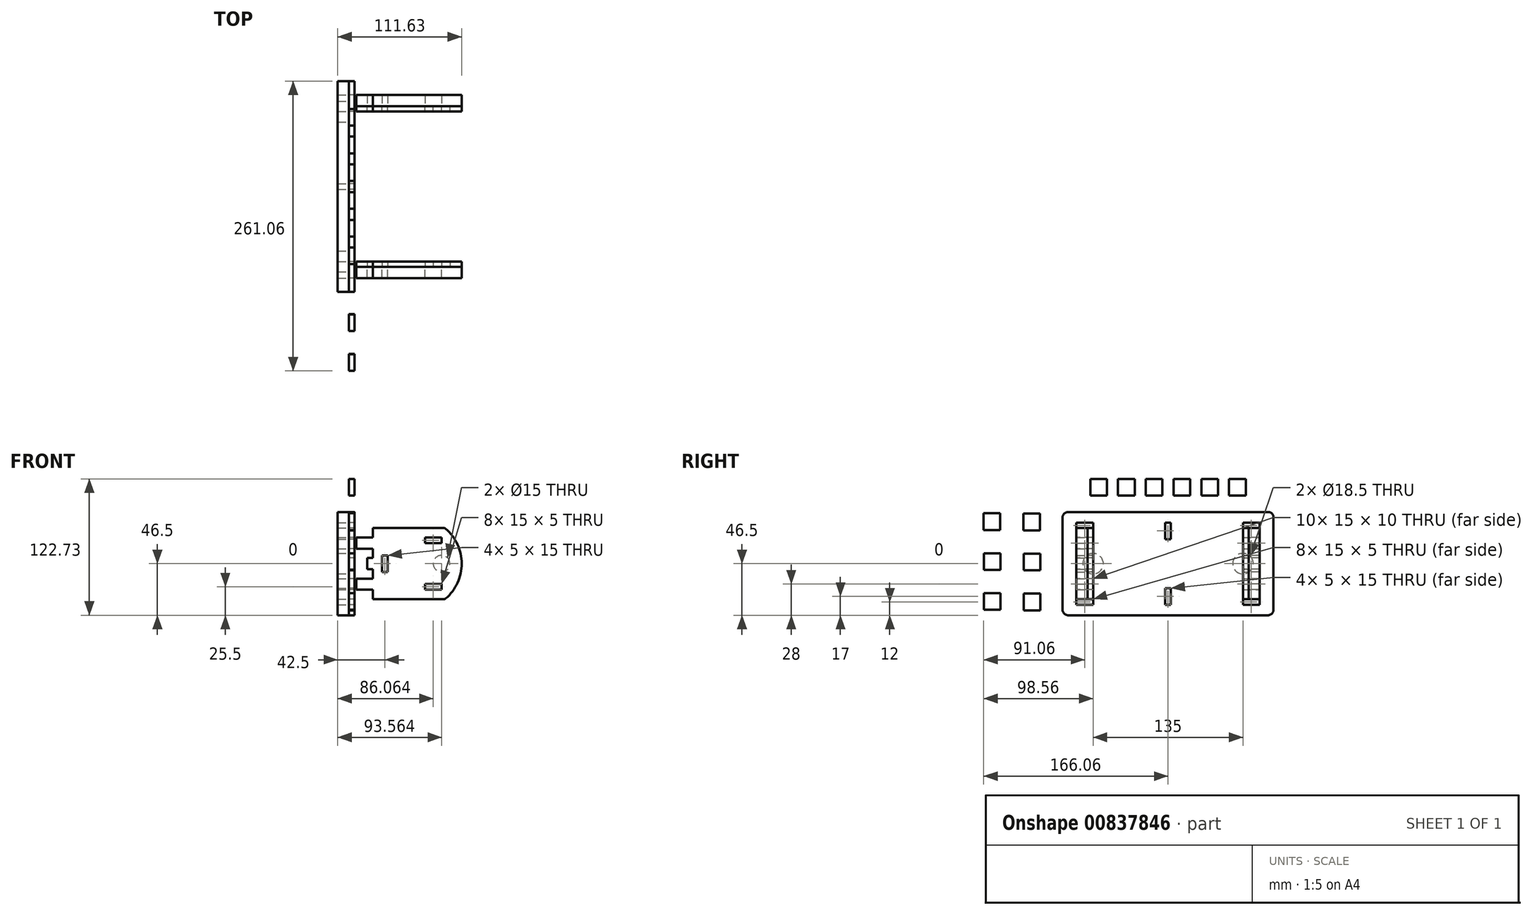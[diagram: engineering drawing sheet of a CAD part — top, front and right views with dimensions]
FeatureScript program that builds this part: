
annotation { "Feature Type Name" : "Feature", "Feature Type Description" : "" }
export const myFeature = defineFeature(function(context is Context, id is Id, definition is map)
    precondition{}
    {
        {
            var Q0;
            Q0=qCreatedBy(makeId("Right.planeOp"),FACE);
            var sketch = newSketch(context, id + "F0", { "sketchPlane" : qUnion([Q0])});
            skLineSegment(sketch, "E0.bottom", {"start": v(90, -46.5) * mm, "end": v(-90, -46.5) * mm});
            skLineSegment(sketch, "E0.top", {"start": v(90, 46.5) * mm, "end": v(-90, 46.5) * mm});
            skLineSegment(sketch, "E0.left", {"start": v(95, -41.5) * mm, "end": v(95, 41.5) * mm});
            skLineSegment(sketch, "E0.right", {"start": v(-95, -41.5) * mm, "end": v(-95, 41.5) * mm});
            skPoint(sketch, "E0.middle", {"position": v(0, 0) * mm});
            skLineSegment(sketch, "E1.bottom", {"start": v(67.5, 23.5) * mm, "end": v(82.5, 23.5) * mm});
            skLineSegment(sketch, "E1.top", {"start": v(67.5, 13.5) * mm, "end": v(82.5, 13.5) * mm});
            skLineSegment(sketch, "E1.left", {"start": v(67.5, 23.5) * mm, "end": v(67.5, 13.5) * mm});
            skLineSegment(sketch, "E1.right", {"start": v(82.5, 23.5) * mm, "end": v(82.5, 13.5) * mm});
            skLineSegment(sketch, "E2.bottom", {"start": v(67.5, -13.5) * mm, "end": v(82.5, -13.5) * mm});
            skLineSegment(sketch, "E2.top", {"start": v(67.5, -23.5) * mm, "end": v(82.5, -23.5) * mm});
            skLineSegment(sketch, "E2.left", {"start": v(67.5, -13.5) * mm, "end": v(67.5, -23.5) * mm});
            skLineSegment(sketch, "E2.right", {"start": v(82.5, -13.5) * mm, "end": v(82.5, -23.5) * mm});
            skLineSegment(sketch, "E3.bottom", {"start": v(-67.5, -13.5) * mm, "end": v(-82.5, -13.5) * mm});
            skLineSegment(sketch, "E3.top", {"start": v(-67.5, -23.5) * mm, "end": v(-82.5, -23.5) * mm});
            skLineSegment(sketch, "E3.left", {"start": v(-67.5, -13.5) * mm, "end": v(-67.5, -23.5) * mm});
            skLineSegment(sketch, "E3.right", {"start": v(-82.5, -13.5) * mm, "end": v(-82.5, -23.5) * mm});
            skLineSegment(sketch, "E4.bottom", {"start": v(-67.5, 13.5) * mm, "end": v(-82.5, 13.5) * mm});
            skLineSegment(sketch, "E4.top", {"start": v(-67.5, 23.5) * mm, "end": v(-82.5, 23.5) * mm});
            skLineSegment(sketch, "E4.left", {"start": v(-67.5, 13.5) * mm, "end": v(-67.5, 23.5) * mm});
            skLineSegment(sketch, "E4.right", {"start": v(-82.5, 13.5) * mm, "end": v(-82.5, 23.5) * mm});
            skPoint(sketch, "E5.visualSharp", {"position": v(-95, 46.5) * mm});
            skArc(sketch, "E5.filletArc", {"start": v(-90, 46.5) * mm, "mid": v(-93.54, 45.04) * mm, "end": v(-95, 41.5) * mm});
            skPoint(sketch, "E6.visualSharp", {"position": v(95, 46.5) * mm});
            skArc(sketch, "E6.filletArc", {"start": v(95, 41.5) * mm, "mid": v(93.54, 45.04) * mm, "end": v(90, 46.5) * mm});
            skPoint(sketch, "E7.visualSharp", {"position": v(95, -46.5) * mm});
            skArc(sketch, "E7.filletArc", {"start": v(90, -46.5) * mm, "mid": v(93.54, -45.04) * mm, "end": v(95, -41.5) * mm});
            skPoint(sketch, "E8.visualSharp", {"position": v(-95, -46.5) * mm});
            skArc(sketch, "E8.filletArc", {"start": v(-95, -41.5) * mm, "mid": v(-93.54, -45.04) * mm, "end": v(-90, -46.5) * mm});
            skCircle(sketch, "E9", {"center": v(-67.5, 0) * mm, "radius": 9.25 * mm});
            skCircle(sketch, "E10", {"center": v(67.5, 0) * mm, "radius": 9.25 * mm});
            skLineSegment(sketch, "E11.bottom", {"start": v(-67.5, 5) * mm, "end": v(-82.5, 5) * mm});
            skLineSegment(sketch, "E11.top", {"start": v(-67.5, -5) * mm, "end": v(-82.5, -5) * mm});
            skLineSegment(sketch, "E11.left", {"start": v(-67.5, 5) * mm, "end": v(-67.5, -5) * mm});
            skLineSegment(sketch, "E11.right", {"start": v(-82.5, 5) * mm, "end": v(-82.5, -5) * mm});
            skLineSegment(sketch, "E12.bottom", {"start": v(82.5, 5) * mm, "end": v(67.5, 5) * mm});
            skLineSegment(sketch, "E12.top", {"start": v(82.5, -5) * mm, "end": v(67.5, -5) * mm});
            skLineSegment(sketch, "E12.left", {"start": v(82.5, 5) * mm, "end": v(82.5, -5) * mm});
            skLineSegment(sketch, "E12.right", {"start": v(67.5, 5) * mm, "end": v(67.5, -5) * mm});
            skLineSegment(sketch, "E13.bottom", {"start": v(-67.5, 32) * mm, "end": v(-82.5, 32) * mm});
            skLineSegment(sketch, "E13.top", {"start": v(-67.5, 37) * mm, "end": v(-82.5, 37) * mm});
            skLineSegment(sketch, "E13.left", {"start": v(-67.5, 32) * mm, "end": v(-67.5, 37) * mm});
            skLineSegment(sketch, "E13.right", {"start": v(-82.5, 32) * mm, "end": v(-82.5, 37) * mm});
            skLineSegment(sketch, "E14.bottom", {"start": v(-82.5, -32) * mm, "end": v(-67.5, -32) * mm});
            skLineSegment(sketch, "E14.top", {"start": v(-82.5, -37) * mm, "end": v(-67.5, -37) * mm});
            skLineSegment(sketch, "E14.left", {"start": v(-82.5, -32) * mm, "end": v(-82.5, -37) * mm});
            skLineSegment(sketch, "E14.right", {"start": v(-67.5, -32) * mm, "end": v(-67.5, -37) * mm});
            skLineSegment(sketch, "E15.bottom", {"start": v(-70, 61.23) * mm, "end": v(-55, 61.23) * mm});
            skLineSegment(sketch, "E15.top", {"start": v(-70, 76.23) * mm, "end": v(-55, 76.23) * mm});
            skLineSegment(sketch, "E15.left", {"start": v(-70, 61.23) * mm, "end": v(-70, 76.23) * mm});
            skLineSegment(sketch, "E15.right", {"start": v(-55, 61.23) * mm, "end": v(-55, 76.23) * mm});
            skLineSegment(sketch, "E16.1.0.0", {"start": v(-45, 76.23) * mm, "end": v(-30, 76.23) * mm});
            skLineSegment(sketch, "E16.1.0.1", {"start": v(-30, 61.23) * mm, "end": v(-30, 76.23) * mm});
            skLineSegment(sketch, "E16.1.0.2", {"start": v(-45, 61.23) * mm, "end": v(-30, 61.23) * mm});
            skLineSegment(sketch, "E16.1.0.3", {"start": v(-45, 61.23) * mm, "end": v(-45, 76.23) * mm});
            skLineSegment(sketch, "E16.2.0.0", {"start": v(-20, 76.23) * mm, "end": v(-5, 76.23) * mm});
            skLineSegment(sketch, "E16.2.0.1", {"start": v(-5, 61.23) * mm, "end": v(-5, 76.23) * mm});
            skLineSegment(sketch, "E16.2.0.2", {"start": v(-20, 61.23) * mm, "end": v(-5, 61.23) * mm});
            skLineSegment(sketch, "E16.2.0.3", {"start": v(-20, 61.23) * mm, "end": v(-20, 76.23) * mm});
            skLineSegment(sketch, "E16.3.0.0", {"start": v(5, 76.23) * mm, "end": v(20, 76.23) * mm});
            skLineSegment(sketch, "E16.3.0.1", {"start": v(20, 61.23) * mm, "end": v(20, 76.23) * mm});
            skLineSegment(sketch, "E16.3.0.2", {"start": v(5, 61.23) * mm, "end": v(20, 61.23) * mm});
            skLineSegment(sketch, "E16.3.0.3", {"start": v(5, 61.23) * mm, "end": v(5, 76.23) * mm});
            skLineSegment(sketch, "E16.direction1", {"start": v(-70, 61.23) * mm, "end": v(-45, 61.23) * mm, "construction": true});
            skLineSegment(sketch, "E17.bottom", {"start": v(67.5, 37) * mm, "end": v(82.5, 37) * mm});
            skLineSegment(sketch, "E17.top", {"start": v(67.5, 32) * mm, "end": v(82.5, 32) * mm});
            skLineSegment(sketch, "E17.left", {"start": v(67.5, 37) * mm, "end": v(67.5, 32) * mm});
            skLineSegment(sketch, "E17.right", {"start": v(82.5, 37) * mm, "end": v(82.5, 32) * mm});
            skLineSegment(sketch, "E18.bottom", {"start": v(67.5, -32) * mm, "end": v(82.5, -32) * mm});
            skLineSegment(sketch, "E18.top", {"start": v(67.5, -37) * mm, "end": v(82.5, -37) * mm});
            skLineSegment(sketch, "E18.left", {"start": v(67.5, -32) * mm, "end": v(67.5, -37) * mm});
            skLineSegment(sketch, "E18.right", {"start": v(82.5, -32) * mm, "end": v(82.5, -37) * mm});
            skLineSegment(sketch, "E19.0.4.0", {"start": v(30, 76.23) * mm, "end": v(45, 76.23) * mm});
            skLineSegment(sketch, "E19.3.4.0", {"start": v(45, 61.23) * mm, "end": v(45, 76.23) * mm});
            skLineSegment(sketch, "E19.6.4.0", {"start": v(30, 61.23) * mm, "end": v(45, 61.23) * mm});
            skLineSegment(sketch, "E19.9.4.0", {"start": v(30, 61.23) * mm, "end": v(30, 76.23) * mm});
            skLineSegment(sketch, "E19.0.5.0", {"start": v(55, 76.23) * mm, "end": v(70, 76.23) * mm});
            skLineSegment(sketch, "E19.3.5.0", {"start": v(70, 61.23) * mm, "end": v(70, 76.23) * mm});
            skLineSegment(sketch, "E19.6.5.0", {"start": v(55, 61.23) * mm, "end": v(70, 61.23) * mm});
            skLineSegment(sketch, "E19.9.5.0", {"start": v(55, 61.23) * mm, "end": v(55, 76.23) * mm});
            skLineSegment(sketch, "E20.bottom", {"start": v(-115.17, 45) * mm, "end": v(-130.17, 45) * mm});
            skLineSegment(sketch, "E20.top", {"start": v(-115.17, 30) * mm, "end": v(-130.17, 30) * mm});
            skLineSegment(sketch, "E20.left", {"start": v(-115.17, 45) * mm, "end": v(-115.17, 30) * mm});
            skLineSegment(sketch, "E20.right", {"start": v(-130.17, 45) * mm, "end": v(-130.17, 30) * mm});
            skLineSegment(sketch, "E21.0.1.0", {"start": v(-115.03, 9) * mm, "end": v(-115.03, -6) * mm});
            skLineSegment(sketch, "E21.0.1.1", {"start": v(-115.03, 9) * mm, "end": v(-130.03, 9) * mm});
            skLineSegment(sketch, "E21.0.1.2", {"start": v(-130.03, 9) * mm, "end": v(-130.03, -6) * mm});
            skLineSegment(sketch, "E21.0.1.3", {"start": v(-115.03, -6) * mm, "end": v(-130.03, -6) * mm});
            skLineSegment(sketch, "E21.1.0.0", {"start": v(-151.06, 45.35) * mm, "end": v(-151.06, 30.35) * mm});
            skLineSegment(sketch, "E21.1.0.1", {"start": v(-151.06, 45.35) * mm, "end": v(-166.06, 45.35) * mm});
            skLineSegment(sketch, "E21.1.0.2", {"start": v(-166.06, 45.35) * mm, "end": v(-166.06, 30.35) * mm});
            skLineSegment(sketch, "E21.1.0.3", {"start": v(-151.06, 30.35) * mm, "end": v(-166.06, 30.35) * mm});
            skLineSegment(sketch, "E21.1.1.0", {"start": v(-150.92, 9.35) * mm, "end": v(-150.92, -5.65) * mm});
            skLineSegment(sketch, "E21.1.1.1", {"start": v(-150.92, 9.35) * mm, "end": v(-165.92, 9.35) * mm});
            skLineSegment(sketch, "E21.1.1.2", {"start": v(-165.92, 9.35) * mm, "end": v(-165.92, -5.65) * mm});
            skLineSegment(sketch, "E21.1.1.3", {"start": v(-150.92, -5.65) * mm, "end": v(-165.92, -5.65) * mm});
            skLineSegment(sketch, "E21.direction1", {"start": v(-115.17, 30) * mm, "end": v(-151.06, 30.35) * mm, "construction": true});
            skLineSegment(sketch, "E21.direction2", {"start": v(-115.17, 30) * mm, "end": v(-115.03, -6) * mm, "construction": true});
            skLineSegment(sketch, "E22.0.0.2", {"start": v(-114.89, -27) * mm, "end": v(-114.89, -42) * mm});
            skLineSegment(sketch, "E22.3.0.2", {"start": v(-114.89, -27) * mm, "end": v(-129.89, -27) * mm});
            skLineSegment(sketch, "E22.6.0.2", {"start": v(-129.89, -27) * mm, "end": v(-129.89, -42) * mm});
            skLineSegment(sketch, "E22.9.0.2", {"start": v(-114.89, -42) * mm, "end": v(-129.89, -42) * mm});
            skLineSegment(sketch, "E22.0.1.2", {"start": v(-150.78, -26.65) * mm, "end": v(-150.78, -41.65) * mm});
            skLineSegment(sketch, "E22.3.1.2", {"start": v(-150.78, -26.65) * mm, "end": v(-165.78, -26.65) * mm});
            skLineSegment(sketch, "E22.6.1.2", {"start": v(-165.78, -26.65) * mm, "end": v(-165.78, -41.65) * mm});
            skLineSegment(sketch, "E22.9.1.2", {"start": v(-150.78, -41.65) * mm, "end": v(-165.78, -41.65) * mm});
            skLineSegment(sketch, "E23.1.0", {"start": v(2.5, 22) * mm, "end": v(2.5, 37) * mm});
            skLineSegment(sketch, "E23.1.1", {"start": v(-2.5, 22) * mm, "end": v(-2.5, 37) * mm});
            skLineSegment(sketch, "E23.1.2", {"start": v(-2.5, 37) * mm, "end": v(2.5, 37) * mm});
            skLineSegment(sketch, "E23.1.3", {"start": v(-2.5, 22) * mm, "end": v(2.5, 22) * mm});
            skLineSegment(sketch, "E23.3.0", {"start": v(-2.5, -22) * mm, "end": v(-2.5, -37) * mm});
            skLineSegment(sketch, "E23.3.1", {"start": v(2.5, -22) * mm, "end": v(2.5, -37) * mm});
            skLineSegment(sketch, "E23.3.2", {"start": v(2.5, -37) * mm, "end": v(-2.5, -37) * mm});
            skLineSegment(sketch, "E23.3.3", {"start": v(2.5, -22) * mm, "end": v(-2.5, -22) * mm});
            skSolve(sketch);
        }
        {
            var Q0;
            Q0=makeQuery(id+"F0.imprint","IMPRINT",FACE,{"disambiguationData":[TD([[makeQuery(id+"F0.imprint","IMPRINT",EDGE,{"derivedFrom":sQuery(id+"F0.wireOp",EDGE,"E0.bottom")}),-1.0]])]});
            var Q1;
            {var subQ5=sQuery(id+"F0.wireOp",EDGE,"E11.left");Q1=makeQuery(id+"F0.imprint","IMPRINT",FACE,{"disambiguationData":[TD([[makeQuery(id+"F0.imprint","IMPRINT",EDGE,{"derivedFrom":subQ5}),1.0]])]});}
            var Q2;
            {var subQ5=sQuery(id+"F0.wireOp",EDGE,"E12.right");Q2=makeQuery(id+"F0.imprint","IMPRINT",FACE,{"disambiguationData":[TD([[makeQuery(id+"F0.imprint","IMPRINT",EDGE,{"derivedFrom":subQ5}),-1.0]])]});}
            var Q3;
            Q3=makeQuery(id+"F0.imprint","IMPRINT",FACE,{"disambiguationData":[TD([[makeQuery(id+"F0.imprint","IMPRINT",EDGE,{"derivedFrom":sQuery(id+"F0.wireOp",EDGE,"E21.1.0.0")}),-1.0]])]});
            var Q4;
            Q4=makeQuery(id+"F0.imprint","IMPRINT",FACE,{"disambiguationData":[TD([[makeQuery(id+"F0.imprint","IMPRINT",EDGE,{"derivedFrom":sQuery(id+"F0.wireOp",EDGE,"E20.bottom")}),1.0]])]});
            var Q5;
            Q5=makeQuery(id+"F0.imprint","IMPRINT",FACE,{"disambiguationData":[TD([[makeQuery(id+"F0.imprint","IMPRINT",EDGE,{"derivedFrom":sQuery(id+"F0.wireOp",EDGE,"E21.1.1.0")}),-1.0]])]});
            var Q6;
            Q6=makeQuery(id+"F0.imprint","IMPRINT",FACE,{"disambiguationData":[TD([[makeQuery(id+"F0.imprint","IMPRINT",EDGE,{"derivedFrom":sQuery(id+"F0.wireOp",EDGE,"E21.0.1.0")}),-1.0]])]});
            var Q7;
            Q7=makeQuery(id+"F0.imprint","IMPRINT",FACE,{"disambiguationData":[TD([[makeQuery(id+"F0.imprint","IMPRINT",EDGE,{"derivedFrom":sQuery(id+"F0.wireOp",EDGE,"E22.0.1.2")}),-1.0]])]});
            var Q8;
            Q8=makeQuery(id+"F0.imprint","IMPRINT",FACE,{"disambiguationData":[TD([[makeQuery(id+"F0.imprint","IMPRINT",EDGE,{"derivedFrom":sQuery(id+"F0.wireOp",EDGE,"E22.0.0.2")}),-1.0]])]});
            var Q9;
            Q9=makeQuery(id+"F0.imprint","IMPRINT",FACE,{"disambiguationData":[TD([[makeQuery(id+"F0.imprint","IMPRINT",EDGE,{"derivedFrom":sQuery(id+"F0.wireOp",EDGE,"E15.bottom")}),1.0]])]});
            var Q10;
            Q10=makeQuery(id+"F0.imprint","IMPRINT",FACE,{"disambiguationData":[TD([[makeQuery(id+"F0.imprint","IMPRINT",EDGE,{"derivedFrom":sQuery(id+"F0.wireOp",EDGE,"E16.1.0.0")}),-1.0]])]});
            var Q11;
            Q11=makeQuery(id+"F0.imprint","IMPRINT",FACE,{"disambiguationData":[TD([[makeQuery(id+"F0.imprint","IMPRINT",EDGE,{"derivedFrom":sQuery(id+"F0.wireOp",EDGE,"E16.2.0.0")}),-1.0]])]});
            var Q12;
            Q12=makeQuery(id+"F0.imprint","IMPRINT",FACE,{"disambiguationData":[TD([[makeQuery(id+"F0.imprint","IMPRINT",EDGE,{"derivedFrom":sQuery(id+"F0.wireOp",EDGE,"E16.3.0.0")}),-1.0]])]});
            var Q13;
            Q13=makeQuery(id+"F0.imprint","IMPRINT",FACE,{"disambiguationData":[TD([[makeQuery(id+"F0.imprint","IMPRINT",EDGE,{"derivedFrom":sQuery(id+"F0.wireOp",EDGE,"E19.0.4.0")}),-1.0]])]});
            var Q14;
            Q14=makeQuery(id+"F0.imprint","IMPRINT",FACE,{"disambiguationData":[TD([[makeQuery(id+"F0.imprint","IMPRINT",EDGE,{"derivedFrom":sQuery(id+"F0.wireOp",EDGE,"E19.0.5.0")}),-1.0]])]});
            extrude(context, id + "F1", {"entities" : qUnion([Q0, Q1, Q2, Q3, Q4, Q5, Q6, Q7, Q8, Q9, Q10, Q11, Q12, Q13, Q14]), "depth" : 5 * mm, "offsetDistance" : 25 * mm});
        }
        {
            var Q0;
            Q0=makeQuery(id+"F0.imprint","IMPRINT",FACE,{"disambiguationData":[TD([[makeQuery(id+"F0.imprint","IMPRINT",EDGE,{"derivedFrom":sQuery(id+"F0.wireOp",EDGE,"E0.bottom")}),-1.0]])]});
            var Q1;
            {var subQ5=sQuery(id+"F0.wireOp",EDGE,"E12.left");Q1=makeQuery(id+"F0.imprint","IMPRINT",FACE,{"disambiguationData":[TD([[makeQuery(id+"F0.imprint","IMPRINT",EDGE,{"derivedFrom":subQ5}),-1.0]])]});}
            var Q2;
            {var subQ5=sQuery(id+"F0.wireOp",EDGE,"E11.right");Q2=makeQuery(id+"F0.imprint","IMPRINT",FACE,{"disambiguationData":[TD([[makeQuery(id+"F0.imprint","IMPRINT",EDGE,{"derivedFrom":subQ5}),1.0]])]});}
            var Q3;
            Q3=makeQuery(id+"F0.imprint","IMPRINT",FACE,{"disambiguationData":[TD([[makeQuery(id+"F0.imprint","IMPRINT",EDGE,{"derivedFrom":sQuery(id+"F0.wireOp",EDGE,"2e16871f-ea5c-4dd4-b328-3b17c4bea811.0.6.0")}),-1.0]])]});
            var Q4;
            Q4=makeQuery(id+"F0.imprint","IMPRINT",FACE,{"disambiguationData":[TD([[makeQuery(id+"F0.imprint","IMPRINT",EDGE,{"derivedFrom":sQuery(id+"F0.wireOp",EDGE,"2e16871f-ea5c-4dd4-b328-3b17c4bea811.0.7.0")}),-1.0]])]});
            var Q5;
            Q5=makeQuery(id+"F0.imprint","IMPRINT",FACE,{"disambiguationData":[TD([[makeQuery(id+"F0.imprint","IMPRINT",EDGE,{"derivedFrom":sQuery(id+"F0.wireOp",EDGE,"2e16871f-ea5c-4dd4-b328-3b17c4bea811.0.8.0")}),-1.0]])]});
            extrude(context, id + "F2", {"entities" : qUnion([Q0, Q1, Q2, Q3, Q4, Q5]), "oppositeDirection" : true, "depth" : 10 * mm, "offsetDistance" : 25 * mm});
        }
        {
            var Q0;
            Q0=qCreatedBy(makeId("Front.planeOp"),FACE);
            cPlane(context, id + "F3", {"entities" : qUnion([Q0]), "cplaneType" : CPlaneType.OFFSET, "offset" : 72.5 * mm, "width" : 150 * mm, "height" : 150 * mm});
        }
        {
            var Q0;
            Q0=qCreatedBy(id+"F3.planeOp",FACE);
            var sketch = newSketch(context, id + "F4", { "sketchPlane" : qUnion([Q0])});
            skLineSegment(sketch, "E24", {"start": v(85.9, 32) * mm, "end": v(21.63, 32) * mm});
            skLineSegment(sketch, "E25", {"start": v(21.63, 32) * mm, "end": v(21.63, 23.5) * mm});
            skLineSegment(sketch, "E26", {"start": v(21.63, 23.5) * mm, "end": v(6.63, 23.5) * mm});
            skLineSegment(sketch, "E27", {"start": v(6.63, 23.5) * mm, "end": v(6.63, 13.5) * mm});
            skLineSegment(sketch, "E28", {"start": v(6.63, 13.5) * mm, "end": v(21.63, 13.5) * mm});
            skLineSegment(sketch, "E29", {"start": v(21.63, -13.5) * mm, "end": v(6.63, -13.5) * mm});
            skLineSegment(sketch, "E30", {"start": v(6.63, -13.5) * mm, "end": v(6.63, -23.5) * mm});
            skLineSegment(sketch, "E31", {"start": v(6.63, -23.5) * mm, "end": v(21.63, -23.5) * mm});
            skLineSegment(sketch, "E32", {"start": v(21.63, -23.5) * mm, "end": v(21.63, -32) * mm});
            skLineSegment(sketch, "E33", {"start": v(21.63, -32) * mm, "end": v(85.9, -32) * mm});
            skPoint(sketch, "E34", {"position": v(101.63, 0) * mm});
            skArc(sketch, "E35", {"start": v(87.2, -31.51) * mm, "mid": v(101.63, 0) * mm, "end": v(87.2, 31.51) * mm});
            skPoint(sketch, "E36.visualSharp", {"position": v(86.63, 32) * mm});
            skArc(sketch, "E36.filletArc", {"start": v(87.2, 31.51) * mm, "mid": v(86.6, 31.87) * mm, "end": v(85.9, 32) * mm});
            skPoint(sketch, "E37.visualSharp", {"position": v(86.63, -32) * mm});
            skArc(sketch, "E37.filletArc", {"start": v(85.9, -32) * mm, "mid": v(86.6, -31.87) * mm, "end": v(87.2, -31.51) * mm});
            skCircle(sketch, "E38", {"center": v(83.56, 0) * mm, "radius": 7.5 * mm});
            skLineSegment(sketch, "E39", {"start": v(21.63, 13.5) * mm, "end": v(21.63, 5) * mm});
            skLineSegment(sketch, "E40", {"start": v(21.63, 5) * mm, "end": v(16.63, 5) * mm});
            skLineSegment(sketch, "E41", {"start": v(16.63, 5) * mm, "end": v(16.63, -5) * mm});
            skLineSegment(sketch, "E42", {"start": v(16.63, -5) * mm, "end": v(21.63, -5) * mm});
            skLineSegment(sketch, "E43", {"start": v(21.63, -5) * mm, "end": v(21.63, -13.5) * mm});
            skLineSegment(sketch, "E44.bottom", {"start": v(83.56, 23.5) * mm, "end": v(68.56, 23.5) * mm});
            skLineSegment(sketch, "E44.top", {"start": v(83.56, 18.5) * mm, "end": v(68.56, 18.5) * mm});
            skLineSegment(sketch, "E44.left", {"start": v(83.56, 23.5) * mm, "end": v(83.56, 18.5) * mm});
            skLineSegment(sketch, "E44.right", {"start": v(68.56, 23.5) * mm, "end": v(68.56, 18.5) * mm});
            skLineSegment(sketch, "E45.bottom", {"start": v(83.56, -18.5) * mm, "end": v(68.56, -18.5) * mm});
            skLineSegment(sketch, "E45.top", {"start": v(83.56, -23.5) * mm, "end": v(68.56, -23.5) * mm});
            skLineSegment(sketch, "E45.left", {"start": v(83.56, -18.5) * mm, "end": v(83.56, -23.5) * mm});
            skLineSegment(sketch, "E45.right", {"start": v(68.56, -18.5) * mm, "end": v(68.56, -23.5) * mm});
            skLineSegment(sketch, "E46.bottom", {"start": v(30, 7.5) * mm, "end": v(35, 7.5) * mm});
            skLineSegment(sketch, "E46.top", {"start": v(30, -7.5) * mm, "end": v(35, -7.5) * mm});
            skLineSegment(sketch, "E46.left", {"start": v(30, 7.5) * mm, "end": v(30, -7.5) * mm});
            skLineSegment(sketch, "E46.right", {"start": v(35, 7.5) * mm, "end": v(35, -7.5) * mm});
            skSolve(sketch);
        }
        {
            var Q0;
            Q0=makeQuery(id+"F4.imprint","IMPRINT",FACE,{"disambiguationData":[TD([[makeQuery(id+"F4.imprint","IMPRINT",EDGE,{"derivedFrom":sQuery(id+"F4.wireOp",EDGE,"E24")}),1.0]])]});
            extrude(context, id + "F5", {"entities" : qUnion([Q0]), "oppositeDirection" : true, "depth" : 5 * mm, "offsetDistance" : 25 * mm});
        }
        {
            var Q0;
            Q0=makeQuery(id+"F4.imprint","IMPRINT",FACE,{"disambiguationData":[TD([[makeQuery(id+"F4.imprint","IMPRINT",EDGE,{"derivedFrom":sQuery(id+"F4.wireOp",EDGE,"E24")}),1.0]])]});
            var Q1;
            Q1=makeQuery(id+"F4.imprint","IMPRINT",FACE,{"disambiguationData":[TD([[makeQuery(id+"F4.imprint","IMPRINT",EDGE,{"derivedFrom":sQuery(id+"F4.wireOp",EDGE,"E38")}),1.0]])]});
            extrude(context, id + "F6", {"entities" : qUnion([Q0, Q1]), "depth" : 10 * mm, "offsetDistance" : 25 * mm});
        }
        {
            var Q0;
            Q0=qCreatedBy(makeId("Top.planeOp"),FACE);
            var sketch = newSketch(context, id + "F7", { "sketchPlane" : qUnion([Q0])});
            skLineSegment(sketch, "E47", {"start": v(0, 0) * mm, "end": v(159.96, 0) * mm, "construction": true});
            skSolve(sketch);
        }
        {
            var Q0;
            Q0=makeQuery(id+"F5.opExtrude","SWEPT_BODY",BODY,{"disambiguationData":[OSD([sQuery(id+"F4.wireOp",EDGE,"E24"),sQuery(id+"F4.wireOp",EDGE,"E25"),sQuery(id+"F4.wireOp",EDGE,"E26"),sQuery(id+"F4.wireOp",EDGE,"E27"),sQuery(id+"F4.wireOp",EDGE,"E28"),sQuery(id+"F4.wireOp",EDGE,"E29"),sQuery(id+"F4.wireOp",EDGE,"E30"),sQuery(id+"F4.wireOp",EDGE,"E31"),sQuery(id+"F4.wireOp",EDGE,"E32"),sQuery(id+"F4.wireOp",EDGE,"E33"),sQuery(id+"F4.wireOp",EDGE,"E35"),sQuery(id+"F4.wireOp",EDGE,"E36.filletArc"),sQuery(id+"F4.wireOp",EDGE,"E37.filletArc"),sQuery(id+"F4.wireOp",EDGE,"E38"),sQuery(id+"F4.wireOp",EDGE,"E39"),sQuery(id+"F4.wireOp",EDGE,"E40"),sQuery(id+"F4.wireOp",EDGE,"E41"),sQuery(id+"F4.wireOp",EDGE,"E42"),sQuery(id+"F4.wireOp",EDGE,"E43"),sQuery(id+"F4.wireOp",EDGE,"E44.bottom"),sQuery(id+"F4.wireOp",EDGE,"E44.top"),sQuery(id+"F4.wireOp",EDGE,"E44.left"),sQuery(id+"F4.wireOp",EDGE,"E44.right"),sQuery(id+"F4.wireOp",EDGE,"E45.bottom"),sQuery(id+"F4.wireOp",EDGE,"E45.top"),sQuery(id+"F4.wireOp",EDGE,"E45.left"),sQuery(id+"F4.wireOp",EDGE,"E45.right"),sQuery(id+"F4.wireOp",EDGE,"E46.bottom"),sQuery(id+"F4.wireOp",EDGE,"E46.top"),sQuery(id+"F4.wireOp",EDGE,"E46.left"),sQuery(id+"F4.wireOp",EDGE,"E46.right")])]});
            var Q1;
            Q1=makeQuery(id+"F6.opExtrude","SWEPT_BODY",BODY,{"disambiguationData":[OSD([sQuery(id+"F4.wireOp",EDGE,"E24"),sQuery(id+"F4.wireOp",EDGE,"E25"),sQuery(id+"F4.wireOp",EDGE,"E26"),sQuery(id+"F4.wireOp",EDGE,"E27"),sQuery(id+"F4.wireOp",EDGE,"E28"),sQuery(id+"F4.wireOp",EDGE,"E29"),sQuery(id+"F4.wireOp",EDGE,"E30"),sQuery(id+"F4.wireOp",EDGE,"E31"),sQuery(id+"F4.wireOp",EDGE,"E32"),sQuery(id+"F4.wireOp",EDGE,"E33"),sQuery(id+"F4.wireOp",EDGE,"E35"),sQuery(id+"F4.wireOp",EDGE,"E36.filletArc"),sQuery(id+"F4.wireOp",EDGE,"E37.filletArc"),sQuery(id+"F4.wireOp",EDGE,"E39"),sQuery(id+"F4.wireOp",EDGE,"E40"),sQuery(id+"F4.wireOp",EDGE,"E41"),sQuery(id+"F4.wireOp",EDGE,"E42"),sQuery(id+"F4.wireOp",EDGE,"E43"),sQuery(id+"F4.wireOp",EDGE,"E44.bottom"),sQuery(id+"F4.wireOp",EDGE,"E44.top"),sQuery(id+"F4.wireOp",EDGE,"E44.left"),sQuery(id+"F4.wireOp",EDGE,"E44.right"),sQuery(id+"F4.wireOp",EDGE,"E45.bottom"),sQuery(id+"F4.wireOp",EDGE,"E45.top"),sQuery(id+"F4.wireOp",EDGE,"E45.left"),sQuery(id+"F4.wireOp",EDGE,"E45.right"),sQuery(id+"F4.wireOp",EDGE,"E46.bottom"),sQuery(id+"F4.wireOp",EDGE,"E46.top"),sQuery(id+"F4.wireOp",EDGE,"E46.left"),sQuery(id+"F4.wireOp",EDGE,"E46.right")])]});
            var Q2;
            Q2=sQuery(id+"F7.wireOp",EDGE,"E47");
            circularPattern(context, id + "F8", {"entities" : qUnion([Q0, Q1]), "axis" : qUnion([Q2]), "angle" : 360 * degree, "instanceCount" : 2, "equalSpace" : true});
        }
    });
